# Revit family: AFX-Cole-LED_39_Pendant-
name_source: partatom
category: Lighting Fixtures
units: mm (PartAtom-declared; Revit-internal decimal feet)

## family parameters
Cut with Voids When Loaded = No
Host = Face
Light Source = Yes
Part Type = Normal
Room Calculation Point = No
Round Connector Dimension = Use Diameter
Shared = No

## types (1)
- COLP39L30D1BK
    Apparent Load = 0 VA
    Assembly Code = D5020200
    Canopy Finish = AFX - Aluminum Black
    Color Filter = 16777215
    Colour Rendering Index = 90CRI
    Cord Finish = AFX - Plastic Black
    Default Elevation = 48"
    Description = Layered Contemporary LED pendant with extruded aluminum housing and 3 sided illumination Suspended by a 9 ft adjustable cable - 39"L x 14 1/2"W x 11"H
    Diffuser Finish = AFX - White Acrylic
    Dimming Lamp Color Temperature Shift = <None>
    Frame Finish = AFX - Aluminum Black
    Height = 11"
    Keynote = 12500
    Length = 39"
    Manufacturer = AFX Inc
    Model = COLP39L30D1BK
    Photometric Web File = COLP39L30D1xx_IES.IES
    Product Documentation Link = https://www.afxinc.com
    Revit File Built By = https://servex-us.com
    Tilt Angle = 0.00°
    Type Comments = Cole
    URL = https://www.afxinc.com
    Voltage = 120 V
    Wattage Comments = 34
    Width = 14 1/2"

## geometry (parser evidence)
native form markers: Sweep x3
no freeform markers — native parametric forms only
